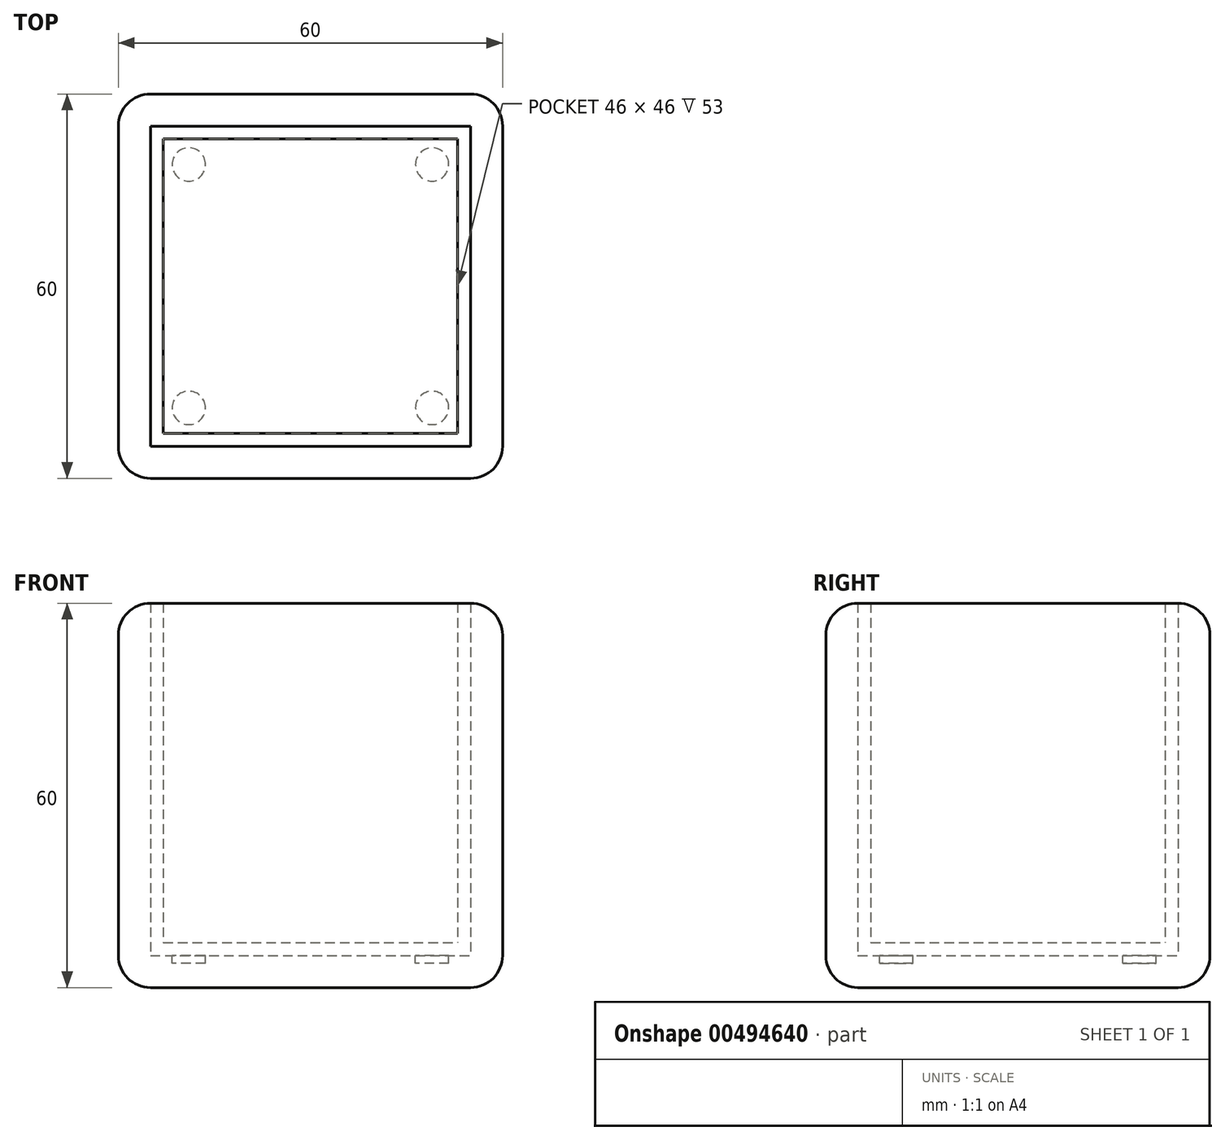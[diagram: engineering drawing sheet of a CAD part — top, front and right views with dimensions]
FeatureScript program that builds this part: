
annotation { "Feature Type Name" : "Feature", "Feature Type Description" : "" }
export const myFeature = defineFeature(function(context is Context, id is Id, definition is map)
    precondition{}
    {
        {
            var Q0;
            Q0=qCreatedBy(makeId("Top.planeOp"),FACE);
            var sketch = newSketch(context, id + "F0", { "sketchPlane" : qUnion([Q0])});
            skLineSegment(sketch, "E0.bottom", {"start": v(-25, 30) * mm, "end": v(25, 30) * mm});
            skLineSegment(sketch, "E0.top", {"start": v(-25, -30) * mm, "end": v(25, -30) * mm});
            skLineSegment(sketch, "E0.left", {"start": v(-30, 25) * mm, "end": v(-30, -25) * mm});
            skLineSegment(sketch, "E0.right", {"start": v(30, 25) * mm, "end": v(30, -25) * mm});
            skPoint(sketch, "E0.middle", {"position": v(0, 0) * mm});
            skPoint(sketch, "E1.visualSharp", {"position": v(30, 30) * mm});
            skArc(sketch, "E1.filletArc", {"start": v(30, 25) * mm, "mid": v(28.54, 28.54) * mm, "end": v(25, 30) * mm});
            skPoint(sketch, "E2.visualSharp", {"position": v(-30, 30) * mm});
            skArc(sketch, "E2.filletArc", {"start": v(-25, 30) * mm, "mid": v(-28.54, 28.54) * mm, "end": v(-30, 25) * mm});
            skPoint(sketch, "E3.visualSharp", {"position": v(-30, -30) * mm});
            skArc(sketch, "E3.filletArc", {"start": v(-30, -25) * mm, "mid": v(-28.54, -28.54) * mm, "end": v(-25, -30) * mm});
            skPoint(sketch, "E4.visualSharp", {"position": v(30, -30) * mm});
            skArc(sketch, "E4.filletArc", {"start": v(25, -30) * mm, "mid": v(28.54, -28.54) * mm, "end": v(30, -25) * mm});
            skSolve(sketch);
        }
        {
            var Q0;
            Q0 = qSketchRegion(id + "F0", true);
            extrude(context, id + "F1", {"entities" : qUnion([Q0]), "depth" : 60 * mm});
        }
        {
            var Q0;
            Q0=makeQuery(id+"F1.opExtrude","CAP_EDGE",EDGE,{"disambiguationData":[OSD([sQuery(id+"F0.wireOp",EDGE,"E3.filletArc")])],"isStart":false});
            var Q1;
            Q1=makeQuery(id+"F1.opExtrude","CAP_EDGE",EDGE,{"disambiguationData":[OSD([sQuery(id+"F0.wireOp",EDGE,"E3.filletArc")])],"isStart":true});
            fillet(context, id + "F2", {"entities" : qUnion([Q0, Q1]), "radius" : 5 * mm, "tangentPropagation" : true, "allowEdgeOverflow" : false});
        }
        {
            var Q0;
            Q0=makeQuery(id+"F1.opExtrude","CAP_FACE",FACE,{"disambiguationData":[OSD([sQuery(id+"F0.wireOp",EDGE,"E0.bottom"),sQuery(id+"F0.wireOp",EDGE,"E0.top"),sQuery(id+"F0.wireOp",EDGE,"E0.left"),sQuery(id+"F0.wireOp",EDGE,"E0.right"),sQuery(id+"F0.wireOp",EDGE,"E1.filletArc"),sQuery(id+"F0.wireOp",EDGE,"E2.filletArc"),sQuery(id+"F0.wireOp",EDGE,"E3.filletArc"),sQuery(id+"F0.wireOp",EDGE,"E4.filletArc")])],"isStart":false});
            shell(context, id + "F3", {"entities" : qUnion([Q0]), "thickness" : 5 * mm});
        }
        {
            var Q0;
            Q0=makeQuery(id+"F3.opShell","OFFSET_FACE",FACE,{"disambiguationData":[OSD([sQuery(id+"F0.wireOp",EDGE,"E0.bottom"),sQuery(id+"F0.wireOp",EDGE,"E0.top"),sQuery(id+"F0.wireOp",EDGE,"E0.left"),sQuery(id+"F0.wireOp",EDGE,"E0.right"),sQuery(id+"F0.wireOp",EDGE,"E1.filletArc"),sQuery(id+"F0.wireOp",EDGE,"E2.filletArc"),sQuery(id+"F0.wireOp",EDGE,"E3.filletArc"),sQuery(id+"F0.wireOp",EDGE,"E4.filletArc")])]});
            var sketch = newSketch(context, id + "F4", { "sketchPlane" : qUnion([Q0])});
            skPoint(sketch, "E5", {"position": v(-19, 0) * mm});
            skPoint(sketch, "E6", {"position": v(19, 0) * mm});
            skPoint(sketch, "E7", {"position": v(19, 19) * mm});
            skPoint(sketch, "E8", {"position": v(19, -19) * mm});
            skPoint(sketch, "E9", {"position": v(-19, 19) * mm});
            skPoint(sketch, "E10", {"position": v(-19, -19) * mm});
            skCircle(sketch, "E11", {"center": v(-19, 19) * mm, "radius": 2.6 * mm});
            skCircle(sketch, "E12", {"center": v(19, 19) * mm, "radius": 2.6 * mm});
            skCircle(sketch, "E13", {"center": v(19, -19) * mm, "radius": 2.6 * mm});
            skCircle(sketch, "E14", {"center": v(-19, -19) * mm, "radius": 2.6 * mm});
            skSolve(sketch);
        }
        {
            var Q0;
            Q0 = qSketchRegion(id + "F4", true);
            extrude(context, id + "F5", {"entities" : qUnion([Q0]), "operationType" : NewBodyOperationType.REMOVE, "oppositeDirection" : true, "depth" : 1.2 * mm});
        }
        {
            var Q0;
            Q0=makeQuery(id+"F3.opShell","OFFSET_FACE",FACE,{"disambiguationData":[OSD([sQuery(id+"F0.wireOp",EDGE,"E0.bottom"),sQuery(id+"F0.wireOp",EDGE,"E0.top"),sQuery(id+"F0.wireOp",EDGE,"E0.left"),sQuery(id+"F0.wireOp",EDGE,"E0.right"),sQuery(id+"F0.wireOp",EDGE,"E1.filletArc"),sQuery(id+"F0.wireOp",EDGE,"E2.filletArc"),sQuery(id+"F0.wireOp",EDGE,"E3.filletArc"),sQuery(id+"F0.wireOp",EDGE,"E4.filletArc")])]});
            var sketch = newSketch(context, id + "F6", { "sketchPlane" : qUnion([Q0])});
            skLineSegment(sketch, "E15.bottom", {"start": v(25, 25) * mm, "end": v(-25, 25) * mm});
            skLineSegment(sketch, "E15.top", {"start": v(25, -25) * mm, "end": v(-25, -25) * mm});
            skLineSegment(sketch, "E15.left", {"start": v(25, 25) * mm, "end": v(25, -25) * mm});
            skLineSegment(sketch, "E15.right", {"start": v(-25, 25) * mm, "end": v(-25, -25) * mm});
            skSolve(sketch);
        }
        {
            var Q0;
            Q0 = qSketchRegion(id + "F6", true);
            extrude(context, id + "F7", {"entities" : qUnion([Q0]), "depth" : 55 * mm});
        }
        {
            var Q0;
            Q0=makeQuery(id+"F7.opExtrude","CAP_FACE",FACE,{"disambiguationData":[OSD([sQuery(id+"F6.wireOp",EDGE,"E15.bottom"),sQuery(id+"F6.wireOp",EDGE,"E15.top"),sQuery(id+"F6.wireOp",EDGE,"E15.left"),sQuery(id+"F6.wireOp",EDGE,"E15.right")])],"isStart":false});
            shell(context, id + "F8", {"entities" : qUnion([Q0]), "thickness" : 2 * mm});
        }
    });
